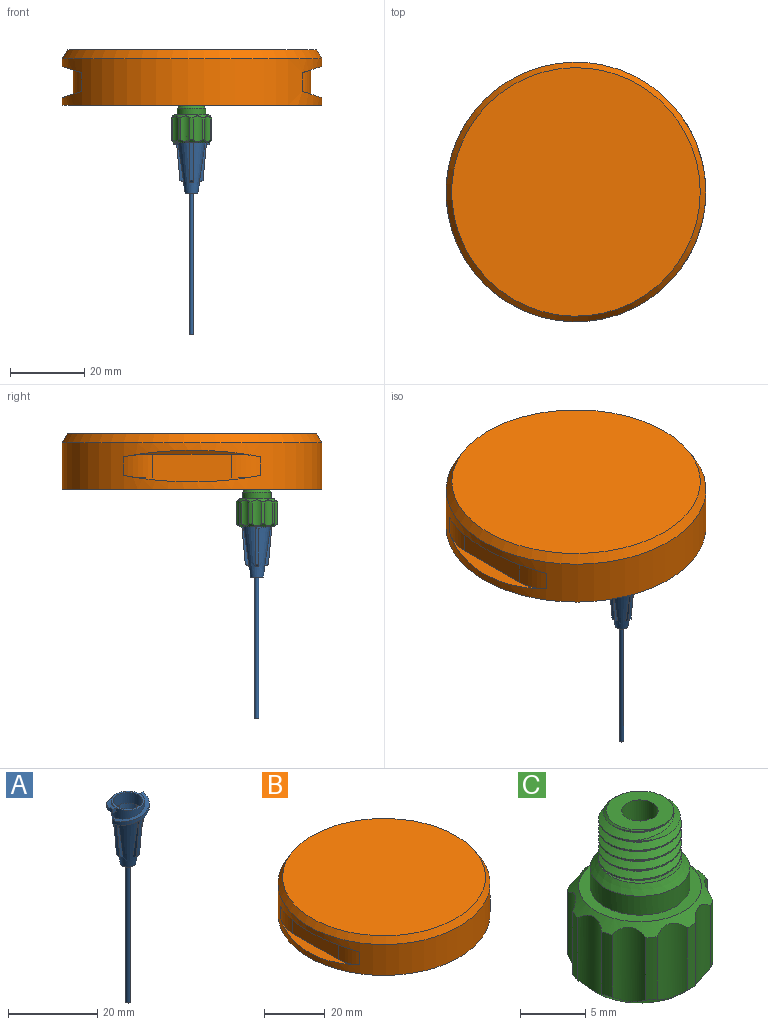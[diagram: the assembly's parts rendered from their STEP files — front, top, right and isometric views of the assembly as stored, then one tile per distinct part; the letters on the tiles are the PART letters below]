
ASSEMBLY  parts=3 mates=1
PART A: 63 faces, bbox 9.5x11x55.1 mm
  f0: cylinder r=3.75mm len=7.5mm, axis (0,0,1), area 25.5mm2, adj f3,f4,f11,f14,f21
  f1: cylinder r=3.75mm len=7.5mm, axis (0,0,1), area 25.5mm2, adj f3,f4,f16,f18,f20
  f2: plane 3.5x3.5mm, normal (0,0,-1), area 8.7mm2, adj f4,f8
  f3: plane 7.5x7.5mm, normal (0,0,1), area 11mm2, adj f0,f1,f5
  f4: cone r=3.75mm half-angle=8.1deg, axis (0,0,1), area 199.4mm2, adj f0,f1,f2,f13,f17,f28,f30,f31
  f5: cylinder r=3.25mm len=6.5mm, axis (0,0,1), area 60.5mm2, adj f3,f7
  f6: plane 2.63x2.63mm, normal (0,0,1), area 4.7mm2, adj f7,f10
  f7: cone r=3.26mm half-angle=8.1deg, axis (0,0,1), area 149.8mm2, adj f5,f6,f24,f25,f26,f27,f38,f39
  f8: cylinder r=0.53mm len=38.1mm, axis (0,0,1), area 127.7mm2, adj f2,f9
  f9: plane 1.07x1.07mm, normal (0,0,-1), area 0.2mm2, adj f8,f10
  f10: cylinder r=0.48mm len=38.6mm, axis (0,0,-1), area 117mm2, adj f6,f9
  f11: plane 1x1mm, normal (0,1,0), area 1mm2, adj f0,f14,f15,f16
  f12: plane 1x1mm, normal (0,1,0), area 0.7mm2, adj f13,f14,f15,f16,f34,f35
  f13: cylinder r=3.75mm len=3.25mm, axis (0,0,-1), area 1.5mm2, adj f4,f12,f14,f33,f35
  f14: bspline ~9.6x9.5mm, area 13.6mm2, adj f0,f11,f12,f13,f15,f33,f34
  f15: cylinder r=4.75mm len=9.5mm, axis (0,0,-1), area 14.9mm2, adj f11,f12,f14,f16
  f16: bspline ~9.6x9.5mm, area 13.7mm2, adj f1,f11,f12,f15
  f17: cylinder r=3.75mm len=3.25mm, axis (0,0,-1), area 1.5mm2, adj f4,f19,f20,f53,f55
  f18: plane 1x1mm, normal (0,-1,0), area 1mm2, adj f1,f20,f21,f22
  f19: plane 1x1mm, normal (0,-1,0), area 0.7mm2, adj f17,f20,f21,f22,f54,f55
  f20: bspline ~9.6x9.5mm, area 13.6mm2, adj f1,f17,f18,f19,f22,f53,f54
  f21: bspline ~9.6x9.5mm, area 13.7mm2, adj f0,f18,f19,f22
  f22: cylinder r=4.75mm len=9.5mm, axis (0,0,-1), area 14.9mm2, adj f18,f19,f20,f21
  f23: plane 11.48x1.7mm, normal (0,-0.99,0.15), area 11.6mm2, adj f24,f25,f26,f27
  f24: plane 11.48x1.79mm, normal (1,0,0), area 1.1mm2, adj f7,f23,f26,f27
  f25: plane 11.48x1.79mm, normal (-1,0,0), area 1.1mm2, adj f7,f23,f26,f27
  f26: plane 1x0.12mm, normal (0,0,1), area 0.1mm2, adj f7,f23,f24,f25
  f27: plane 1x0.2mm, normal (0,0.49,-0.87), area 0.2mm2, adj f7,f23,f24,f25
  f28: plane 1.02x1mm, normal (0,0.49,-0.87), area 1.1mm2, adj f4,f29,f31,f32
  f29: plane 10.52x1mm, normal (0,1,-0.09), area 10.6mm2, adj f28,f30,f31,f32
  f30: plane 1x0.36mm, normal (0,0,1), area 0.3mm2, adj f4,f29,f31,f32
  f31: plane 11.1x1.97mm, normal (1,0,0), area 7mm2, adj f4,f28,f29,f30
  f32: plane 11.1x1.97mm, normal (-1,0,0), area 7mm2, adj f4,f28,f29,f30
  f33: plane 11.1x1.89mm, normal (0,-1,0), area 6.8mm2, adj f4,f13,f14,f34,f35,f37
  f34: plane 10.54x1.02mm, normal (-1,0,-0.09), area 10.1mm2, adj f12,f14,f33,f35,f36,f37
  f35: plane 1x0.36mm, normal (0,0,1), area 0.2mm2, adj f4,f12,f13,f33,f34,f36
  f36: plane 11.1x1.97mm, normal (0,1,0), area 7mm2, adj f4,f34,f35,f37
  f37: plane 1.02x1mm, normal (-0.49,0,-0.87), area 1.1mm2, adj f4,f33,f34,f36
  f38: plane 1x0.2mm, normal (-0.49,0,-0.87), area 0.2mm2, adj f7,f39,f41,f42
  f39: plane 11.48x1.79mm, normal (0,1,0), area 1.1mm2, adj f7,f38,f40,f42
  f40: plane 1x0.12mm, normal (0,0,1), area 0.1mm2, adj f7,f39,f41,f42
  f41: plane 11.48x1.79mm, normal (0,-1,0), area 1.1mm2, adj f7,f38,f40,f42
  f42: plane 11.48x1.7mm, normal (0.99,0,0.15), area 11.6mm2, adj f38,f39,f40,f41
  f43: plane 11.48x1.7mm, normal (0,0.99,0.15), area 11.6mm2, adj f44,f45,f46,f47
  f44: plane 11.48x1.79mm, normal (-1,0,0), area 1.1mm2, adj f7,f43,f46,f47
  f45: plane 11.48x1.79mm, normal (1,0,0), area 1.1mm2, adj f7,f43,f46,f47
  f46: plane 1x0.12mm, normal (0,0,1), area 0.1mm2, adj f7,f43,f44,f45
  f47: plane 1x0.2mm, normal (0,-0.49,-0.87), area 0.2mm2, adj f7,f43,f44,f45
  f48: plane 1.02x1mm, normal (0,-0.49,-0.87), area 1.1mm2, adj f4,f49,f51,f52
  f49: plane 10.52x1mm, normal (0,-1,-0.09), area 10.6mm2, adj f48,f50,f51,f52
  f50: plane 1x0.36mm, normal (0,0,1), area 0.3mm2, adj f4,f49,f51,f52
  f51: plane 11.1x1.97mm, normal (-1,0,0), area 7mm2, adj f4,f48,f49,f50
  f52: plane 11.1x1.97mm, normal (1,0,0), area 7mm2, adj f4,f48,f49,f50
  f53: plane 11.1x1.89mm, normal (0,1,0), area 6.8mm2, adj f4,f17,f20,f54,f55,f57
  f54: plane 10.54x1.02mm, normal (1,0,-0.09), area 10.1mm2, adj f19,f20,f53,f55,f56,f57
  f55: plane 1x0.36mm, normal (0,0,1), area 0.2mm2, adj f4,f17,f19,f53,f54,f56
  f56: plane 11.1x1.97mm, normal (0,-1,0), area 7mm2, adj f4,f54,f55,f57
  f57: plane 1.04x1.02mm, normal (0.49,0,-0.87), area 1.1mm2, adj f4,f53,f54,f56
  f58: plane 1.02x0.23mm, normal (0.49,0,-0.87), area 0.2mm2, adj f7,f59,f61,f62
  f59: plane 11.48x1.79mm, normal (0,-1,0), area 1.1mm2, adj f7,f58,f60,f62
  f60: plane 1x0.12mm, normal (0,0,1), area 0.1mm2, adj f7,f59,f61,f62
  f61: plane 11.48x1.79mm, normal (0,1,0), area 1.1mm2, adj f7,f58,f60,f62
  f62: plane 11.48x1.7mm, normal (-0.99,0,0.15), area 11.6mm2, adj f58,f59,f60,f61
PART B: 14 faces, bbox 70x70x15 mm
  f0: cylinder r=35mm len=70mm, axis (0,0,-1), area 2180.2mm2, adj f2,f4,f5,f7,f8,f9,f10,f11
  f1: plane 67x67mm, normal (0,0,1), area 3525.7mm2, adj f13
  f2: plane 70x70mm, normal (0,0,-1), area 3848.5mm2, adj f0
  f3: plane 21.07x6.5mm, normal (1,0,0), area 137mm2, adj f4,f5,f11,f12
  f4: plane 36.87x5.25mm, normal (0.32,0,0.95), area 62.9mm2, adj f0,f3,f11,f12
  f5: plane 36.87x5.25mm, normal (0.32,0,-0.95), area 62.9mm2, adj f0,f3,f11,f12
  f6: plane 21.07x6.5mm, normal (-1,0,0), area 137mm2, adj f7,f8,f9,f10
  f7: plane 36.87x5.25mm, normal (-0.32,0,-0.95), area 62.9mm2, adj f0,f6,f9,f10
  f8: plane 36.87x5.25mm, normal (-0.32,0,0.95), area 62.9mm2, adj f0,f6,f9,f10
  f9: cylinder r=15mm len=7.9mm, axis (0,0,-1), area 49.9mm2, adj f0,f6,f7,f8
  f10: cylinder r=15mm len=7.9mm, axis (0,0,-1), area 49.9mm2, adj f0,f6,f7,f8
  f11: cylinder r=15mm len=7.9mm, axis (0,0,-1), area 49.9mm2, adj f0,f3,f4,f5
  f12: cylinder r=15mm len=7.9mm, axis (0,0,-1), area 49.9mm2, adj f0,f3,f4,f5
  f13: cone r=33.5mm half-angle=31deg, axis (0,0,-1), area 627.4mm2, adj f0,f1
PART C: 38 faces, bbox 11.5x11.5x16.8 mm
  f0: cone r=4.7mm half-angle=45deg, axis (0,0,-1), area 27mm2, adj f10,f11,f12,f13,f14,f15,f16,f17
  f1: cone r=5.59mm half-angle=45deg, axis (0,0,1), area 27mm2, adj f10,f11,f12,f13,f14,f15,f16,f17
  f2: cone r=2.59mm half-angle=45deg, axis (0,0,-1), area 7.6mm2, adj f9,f32,f33,f34
  f3: cylinder r=1.4mm len=15.88mm, axis (0,0,1), area 139.3mm2, adj f32,f37
  f4: cylinder r=3.82mm len=7.63mm, axis (0,0,-1), area 42.5mm2, adj f7,f30
  f5: cone r=2.06mm half-angle=1deg, axis (0,0,1), area 102.1mm2, adj f36,f37
  f6: cylinder r=3.82mm len=7.63mm, axis (0,0,-1), area 155.9mm2, adj f31,f36
  f7: cone r=3.82mm half-angle=39.9deg, axis (0,0,-1), area 22mm2, adj f4,f9,f35
  f8: cylinder r=2.59mm len=5.17mm, axis (0,0,-1), area 9.3mm2, adj f32,f33,f34,f35
  f9: cylinder r=3.17mm len=6.35mm, axis (0,0,1), area 9mm2, adj f2,f7,f33,f34
  f10: cylinder r=2.31mm len=6.96mm, axis (0,0,1), area 17.8mm2, adj f0,f1,f24,f25
  f11: cylinder r=2.31mm len=5.85mm, axis (0,0,1), area 16.2mm2, adj f0,f1,f12,f29
  f12: cylinder r=5.59mm len=5.85mm, axis (0,0,1), area 5.1mm2, adj f0,f1,f11,f13
  f13: cylinder r=2.31mm len=5.85mm, axis (0,0,1), area 16.2mm2, adj f0,f1,f12,f14
  f14: cylinder r=5.59mm len=5.85mm, axis (0,0,1), area 5.1mm2, adj f0,f1,f13,f15
  f15: cylinder r=2.31mm len=5.85mm, axis (0,0,1), area 16.2mm2, adj f0,f1,f14,f16
  f16: cylinder r=5.59mm len=5.85mm, axis (0,0,1), area 5.1mm2, adj f0,f1,f15,f17
  f17: cylinder r=2.31mm len=5.85mm, axis (0,0,1), area 16.2mm2, adj f0,f1,f16,f18
  f18: cylinder r=5.59mm len=5.85mm, axis (0,0,1), area 5.1mm2, adj f0,f1,f17,f19
  f19: cylinder r=2.31mm len=5.85mm, axis (0,0,1), area 16.2mm2, adj f0,f1,f18,f20
  f20: cylinder r=5.59mm len=5.85mm, axis (0,0,1), area 5.1mm2, adj f0,f1,f19,f21
  f21: cylinder r=2.31mm len=5.85mm, axis (0,0,1), area 16.2mm2, adj f0,f1,f20,f22
  f22: cylinder r=5.59mm len=5.85mm, axis (0,0,1), area 5.1mm2, adj f0,f1,f21,f23
  f23: cylinder r=2.31mm len=5.85mm, axis (0,0,1), area 16.2mm2, adj f0,f1,f22,f24
  f24: cylinder r=5.59mm len=5.85mm, axis (0,0,1), area 5.1mm2, adj f0,f1,f10,f23
  f25: cylinder r=5.59mm len=5.85mm, axis (0,0,1), area 5.1mm2, adj f0,f1,f10,f26
  f26: cylinder r=2.31mm len=5.85mm, axis (0,0,1), area 16.2mm2, adj f0,f1,f25,f27
  f27: cylinder r=5.59mm len=5.85mm, axis (0,0,1), area 5.1mm2, adj f0,f1,f26,f28
  f28: cylinder r=2.31mm len=5.85mm, axis (0,0,1), area 16.2mm2, adj f0,f1,f27,f29
  f29: cylinder r=5.59mm len=5.85mm, axis (0,0,1), area 5.1mm2, adj f0,f1,f11,f28
  f30: plane 9.4x9.4mm, normal (0,0,1), area 23.7mm2, adj f0,f4
  f31: plane 9.4x9.4mm, normal (0,0,-1), area 23.7mm2, adj f1,f6
  f32: plane 5.17x5.17mm, normal (0,0,1), area 14.9mm2, adj f2,f3,f8
  f33: bspline ~6.35x6.34mm, area 48.8mm2, adj f2,f8,f9,f35
  f34: bspline ~6.35x6.34mm, area 58mm2, adj f2,f8,f9,f35
  f35: plane 6.71x6.6mm, normal (0,0,1), area 5.5mm2, adj f7,f8,f33,f34
  f36: plane 7.63x7.63mm, normal (0,0,-1), area 30.7mm2, adj f5,f6
  f37: plane 4.11x4.11mm, normal (0,0,-1), area 7.2mm2, adj f3,f5
PLACE A rot(axis=(-1,0,0),0deg) t=(-0.13,-17.49,-21.66)mm
PLACE B rot(axis=(-0.52,-0.12,-0.85),0deg) t=(0,0,-15)mm
PLACE C rot(axis=(-1,0,0),0deg) t=(-0.13,-17.49,-18.37)mm
MATE fastened C.f3 <-> A.f0  axis (0,0,-1) through (-0.13,-17.49,-18.66)mm
